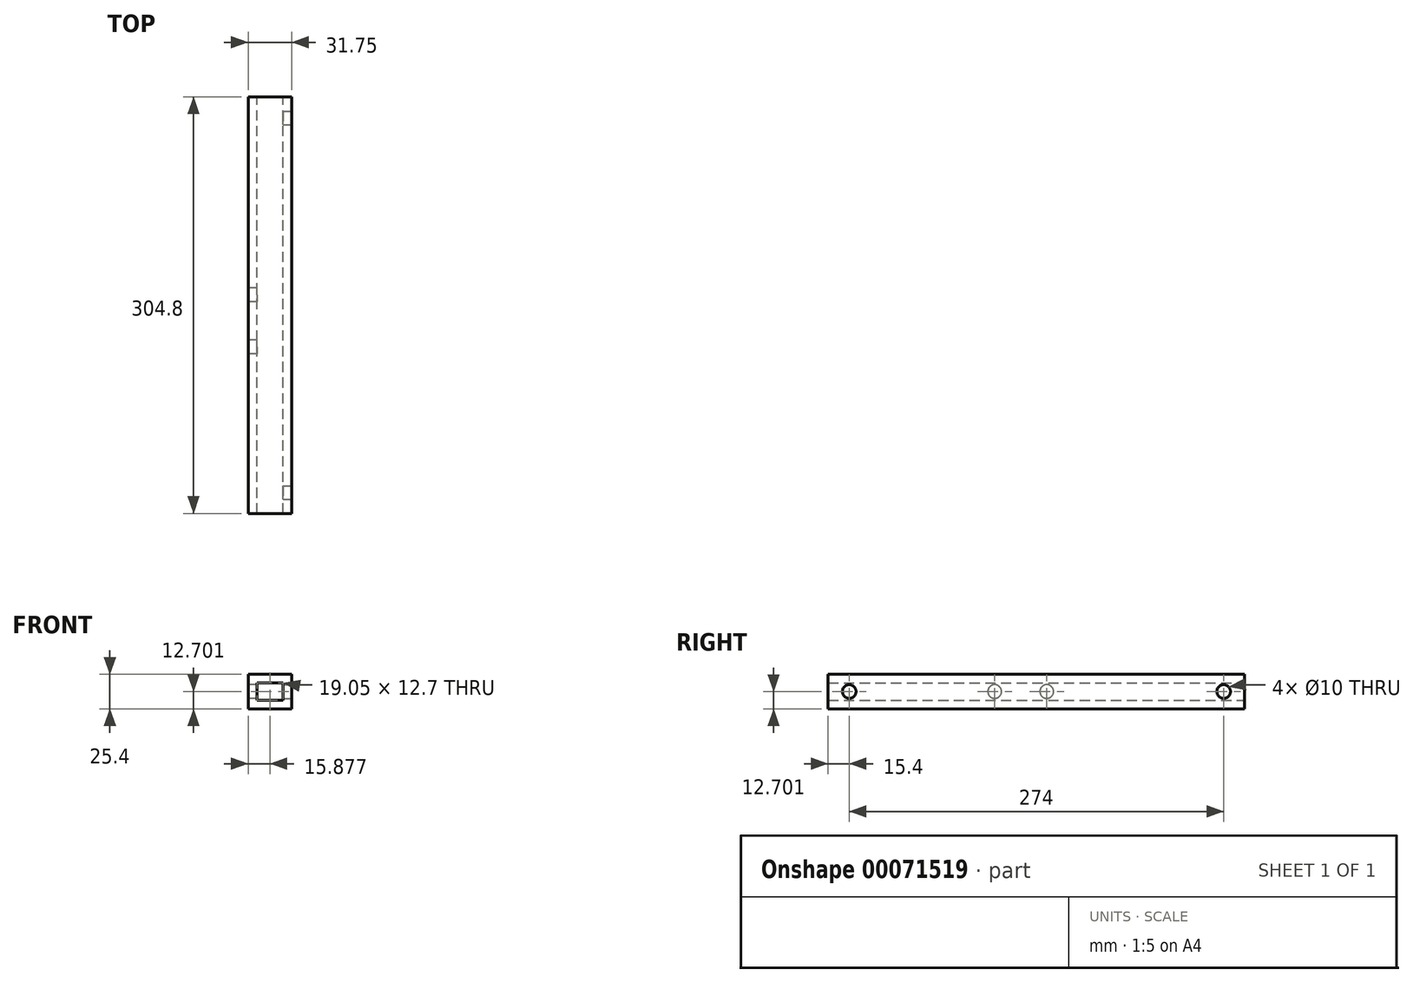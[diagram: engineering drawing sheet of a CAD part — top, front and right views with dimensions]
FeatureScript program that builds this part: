
annotation { "Feature Type Name" : "Feature", "Feature Type Description" : "" }
export const myFeature = defineFeature(function(context is Context, id is Id, definition is map)
    precondition{}
    {
        {
            var Q0;
            Q0=qCreatedBy(makeId("Front.planeOp"),FACE);
            var sketch = newSketch(context, id + "F0", { "sketchPlane" : qUnion([Q0])});
            skLineSegment(sketch, "E0.bottom", {"start": v(-14.24, 7.25) * mm, "end": v(17.51, 7.25) * mm});
            skLineSegment(sketch, "E0.top", {"start": v(-14.24, -18.15) * mm, "end": v(17.51, -18.15) * mm});
            skLineSegment(sketch, "E0.left", {"start": v(-14.24, 7.25) * mm, "end": v(-14.24, -18.15) * mm});
            skLineSegment(sketch, "E0.right", {"start": v(17.51, 7.25) * mm, "end": v(17.51, -18.15) * mm});
            skLineSegment(sketch, "E1.bottom", {"start": v(-7.89, 0.9) * mm, "end": v(11.16, 0.9) * mm});
            skLineSegment(sketch, "E1.top", {"start": v(-7.89, -11.8) * mm, "end": v(11.16, -11.8) * mm});
            skLineSegment(sketch, "E1.left", {"start": v(-7.89, 0.9) * mm, "end": v(-7.89, -11.8) * mm});
            skLineSegment(sketch, "E1.right", {"start": v(11.16, 0.9) * mm, "end": v(11.16, -11.8) * mm});
            skSolve(sketch);
        }
        {
            var Q0;
            Q0 = qSketchRegion(id + "F0", true);
            extrude(context, id + "F1", {"entities" : qUnion([Q0]), "depth" : 304.8 * mm});
        }
        {
            var Q0;
            Q0=makeQuery(id+"F1.opExtrude","SWEPT_FACE",FACE,{"disambiguationData":[OSD([sQuery(id+"F0.wireOp",EDGE,"E0.right")])]});
            var sketch = newSketch(context, id + "F2", { "sketchPlane" : qUnion([Q0])});
            skCircle(sketch, "E2", {"center": v(-15.4, -5.45) * mm, "radius": 5 * mm});
            skCircle(sketch, "E3", {"center": v(-289.4, -5.45) * mm, "radius": 5 * mm});
            skSolve(sketch);
        }
        {
            var Q0;
            Q0 = qSketchRegion(id + "F2", true);
            extrude(context, id + "F3", {"entities" : qUnion([Q0]), "operationType" : NewBodyOperationType.REMOVE, "oppositeDirection" : true, "depth" : 25.4 * mm});
        }
        {
            var Q0;
            Q0=makeQuery(id+"F1.opExtrude","SWEPT_FACE",FACE,{"disambiguationData":[OSD([sQuery(id+"F0.wireOp",EDGE,"E0.left")])]});
            var sketch = newSketch(context, id + "F4", { "sketchPlane" : qUnion([Q0])});
            skCircle(sketch, "E4", {"center": v(144.87, -5.45) * mm, "radius": 5 * mm});
            skCircle(sketch, "E5", {"center": v(182.97, -5.45) * mm, "radius": 5 * mm});
            skSolve(sketch);
        }
        {
            var Q0;
            Q0 = qSketchRegion(id + "F4", true);
            extrude(context, id + "F5", {"entities" : qUnion([Q0]), "operationType" : NewBodyOperationType.REMOVE, "oppositeDirection" : true, "depth" : 12.7 * mm});
        }
    });
